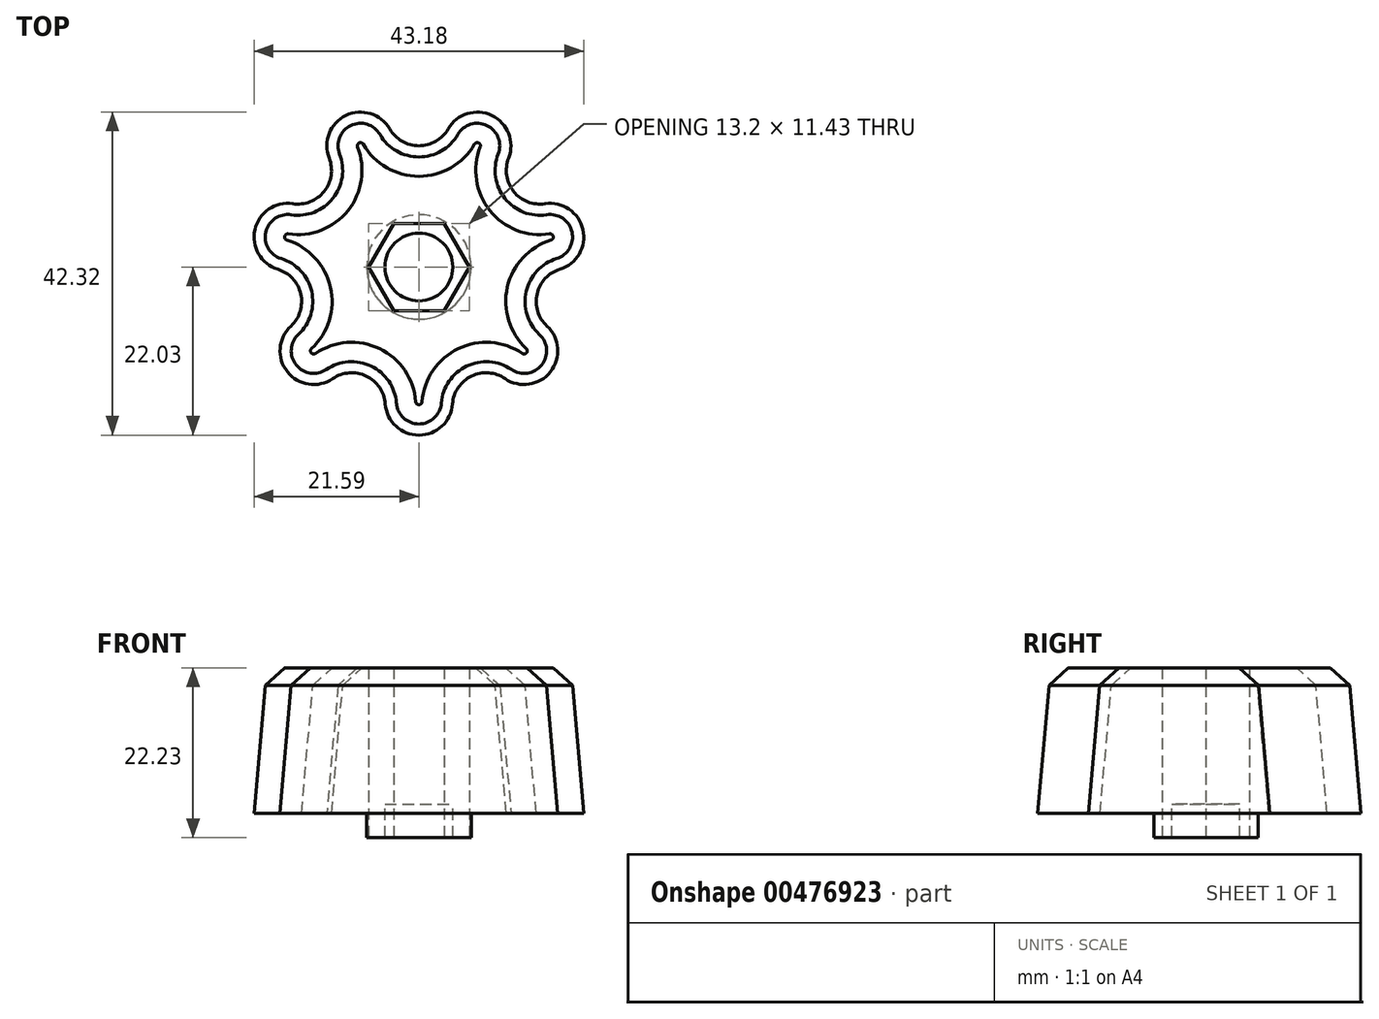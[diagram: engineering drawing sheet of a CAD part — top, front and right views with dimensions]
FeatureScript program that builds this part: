
annotation { "Feature Type Name" : "Feature", "Feature Type Description" : "" }
export const myFeature = defineFeature(function(context is Context, id is Id, definition is map)
    precondition{}
    {
        {
            var Q0;
            Q0=qCreatedBy(makeId("Top.planeOp"),FACE);
            var sketch = newSketch(context, id + "F0", { "sketchPlane" : qUnion([Q0])});
            skCircle(sketch, "E0.cCircle", {"center": v(0, 0) * mm, "radius": 5.72 * mm, "construction": true});
            skLineSegment(sketch, "E0.0", {"start": v(-3.3, 5.72) * mm, "end": v(3.3, 5.72) * mm});
            skLineSegment(sketch, "E0.1", {"start": v(3.3, 5.72) * mm, "end": v(6.6, 0) * mm});
            skLineSegment(sketch, "E0.2", {"start": v(6.6, 0) * mm, "end": v(3.3, -5.71) * mm});
            skLineSegment(sketch, "E0.3", {"start": v(3.3, -5.72) * mm, "end": v(-3.3, -5.72) * mm});
            skLineSegment(sketch, "E0.4", {"start": v(-3.3, -5.72) * mm, "end": v(-6.6, 0) * mm});
            skLineSegment(sketch, "E0.5", {"start": v(-6.6, 0) * mm, "end": v(-3.3, 5.72) * mm});
            skPoint(sketch, "E0.0.midPoint", {"position": v(0, 5.72) * mm});
            skCircle(sketch, "E1.cCircle", {"center": v(0, 0) * mm, "radius": 15.88 * mm, "construction": true});
            skLineSegment(sketch, "E1.0", {"start": v(-7.64, 15.87) * mm, "end": v(7.64, 15.87) * mm, "construction": true});
            skLineSegment(sketch, "E1.1", {"start": v(7.64, 15.88) * mm, "end": v(17.18, 3.92) * mm, "construction": true});
            skLineSegment(sketch, "E1.2", {"start": v(17.18, 3.92) * mm, "end": v(13.78, -10.99) * mm, "construction": true});
            skLineSegment(sketch, "E1.3", {"start": v(13.78, -10.99) * mm, "end": v(0, -17.62) * mm, "construction": true});
            skLineSegment(sketch, "E1.4", {"start": v(0, -17.62) * mm, "end": v(-13.78, -10.99) * mm, "construction": true});
            skLineSegment(sketch, "E1.5", {"start": v(-13.78, -10.99) * mm, "end": v(-17.18, 3.92) * mm, "construction": true});
            skLineSegment(sketch, "E1.6", {"start": v(-17.18, 3.92) * mm, "end": v(-7.64, 15.87) * mm, "construction": true});
            skPoint(sketch, "E1.0.midPoint", {"position": v(0, 15.87) * mm});
            skCircle(sketch, "E2", {"center": v(-7.64, 15.87) * mm, "radius": 4.41 * mm});
            skCircle(sketch, "E3", {"center": v(7.64, 15.87) * mm, "radius": 4.41 * mm});
            skCircle(sketch, "E4", {"center": v(17.18, 3.92) * mm, "radius": 4.41 * mm});
            skCircle(sketch, "E5", {"center": v(13.78, -10.99) * mm, "radius": 4.41 * mm});
            skCircle(sketch, "E6", {"center": v(0, -17.62) * mm, "radius": 4.41 * mm});
            skCircle(sketch, "E7", {"center": v(-13.78, -10.99) * mm, "radius": 4.41 * mm});
            skCircle(sketch, "E8", {"center": v(-17.18, 3.92) * mm, "radius": 4.41 * mm});
            skArc(sketch, "E9", {"start": v(-16.52, 8.29) * mm, "mid": v(-12.41, 9.9) * mm, "end": v(-11.75, 14.26) * mm});
            skArc(sketch, "E10", {"start": v(-3.82, 18.08) * mm, "mid": v(0, 15.87) * mm, "end": v(3.82, 18.08) * mm});
            skArc(sketch, "E11", {"start": v(11.75, 14.26) * mm, "mid": v(12.41, 9.9) * mm, "end": v(16.52, 8.29) * mm});
            skArc(sketch, "E12", {"start": v(18.48, -0.3) * mm, "mid": v(15.48, -3.53) * mm, "end": v(16.78, -7.75) * mm});
            skArc(sketch, "E13", {"start": v(11.29, -14.63) * mm, "mid": v(6.89, -14.3) * mm, "end": v(4.4, -17.95) * mm});
            skArc(sketch, "E14", {"start": v(-4.4, -17.95) * mm, "mid": v(-6.89, -14.3) * mm, "end": v(-11.29, -14.63) * mm});
            skArc(sketch, "E15", {"start": v(-16.78, -7.75) * mm, "mid": v(-15.48, -3.53) * mm, "end": v(-18.48, -0.3) * mm});
            skCircle(sketch, "E16", {"center": v(0, 0) * mm, "radius": 20.29 * mm, "construction": true});
            skCircle(sketch, "E17", {"center": v(0, 0) * mm, "radius": 4.45 * mm});
            skCircle(sketch, "E18", {"center": v(0, 0) * mm, "radius": 9.53 * mm});
            skSolve(sketch);
        }
        {
            var Q0;
            Q0 = qSketchRegion(id + "F0", true);
            var Q1;
            Q1=makeQuery(id+"F0.imprint","IMPRINT",FACE,{"disambiguationData":[TD([[makeQuery(id+"F0.imprint","IMPRINT",EDGE,{"derivedFrom":sQuery(id+"F0.wireOp",EDGE,"E0.0")}),1.0]])]});
            extrude(context, id + "F1", {"entities" : qUnion([Q0, Q1]), "depth" : 19.05 * mm, "hasDraft" : true, "draftAngle" : 5 * degree, "draftPullDirection" : true});
        }
        {
            var Q0;
            Q0=makeQuery(id+"F0.imprint","IMPRINT",FACE,{"disambiguationData":[TD([[makeQuery(id+"F0.imprint","IMPRINT",EDGE,{"derivedFrom":sQuery(id+"F0.wireOp",EDGE,"E0.0")}),1.0]])]});
            var Q1;
            Q1=makeQuery(id+"F1.opExtrude","CAP_FACE",FACE,{"disambiguationData":[OSD([sQuery(id+"F0.wireOp",EDGE,"E0.0"),sQuery(id+"F0.wireOp",EDGE,"E0.1"),sQuery(id+"F0.wireOp",EDGE,"E0.2"),sQuery(id+"F0.wireOp",EDGE,"E0.3"),sQuery(id+"F0.wireOp",EDGE,"E0.4"),sQuery(id+"F0.wireOp",EDGE,"E0.5"),sQuery(id+"F0.wireOp",EDGE,"E2"),sQuery(id+"F0.wireOp",EDGE,"E3"),sQuery(id+"F0.wireOp",EDGE,"E4"),sQuery(id+"F0.wireOp",EDGE,"E5"),sQuery(id+"F0.wireOp",EDGE,"E6"),sQuery(id+"F0.wireOp",EDGE,"E7"),sQuery(id+"F0.wireOp",EDGE,"E8"),sQuery(id+"F0.wireOp",EDGE,"E9"),sQuery(id+"F0.wireOp",EDGE,"E10"),sQuery(id+"F0.wireOp",EDGE,"E11"),sQuery(id+"F0.wireOp",EDGE,"E12"),sQuery(id+"F0.wireOp",EDGE,"E13"),sQuery(id+"F0.wireOp",EDGE,"E14"),sQuery(id+"F0.wireOp",EDGE,"E15")])],"isStart":false});
            extrude(context, id + "F2", {"entities" : qUnion([Q0]), "operationType" : NewBodyOperationType.ADD, "endBound" : BoundingType.UP_TO_SURFACE, "endBoundEntityFace" : qUnion([Q1]), "depth" : 25.4 * mm});
        }
        {
            var Q0;
            Q0=makeQuery(id+"F1.opExtrude","CAP_EDGE",EDGE,{"disambiguationData":[OSD([sQuery(id+"F0.wireOp",EDGE,"E6")])],"isStart":false});
            chamfer(context, id + "F3", {"entities" : qUnion([Q0]), "width" : 2.54 * mm, "tangentPropagation" : true});
        }
        {
            var Q0;
            {var subQ0=sQuery(id+"F0.wireOp",EDGE,"E0.5");var subQ1=sQuery(id+"F0.wireOp",EDGE,"E0.4");var subQ2=sQuery(id+"F0.wireOp",EDGE,"E0.3");var subQ3=sQuery(id+"F0.wireOp",EDGE,"E0.2");var subQ4=sQuery(id+"F0.wireOp",EDGE,"E0.1");var subQ5=sQuery(id+"F0.wireOp",EDGE,"E0.0");Q0=makeQuery(id+"FAqkvu2JH1cbPXJ_1.boolean.opBoolean","MERGE",FACE,{"derivedFrom":[makeQuery(id+"F1.opExtrude","CAP_FACE",FACE,{"disambiguationData":[OSD([subQ5,subQ4,subQ3,subQ2,subQ1,subQ0,sQuery(id+"F0.wireOp",EDGE,"E2"),sQuery(id+"F0.wireOp",EDGE,"E3"),sQuery(id+"F0.wireOp",EDGE,"E4"),sQuery(id+"F0.wireOp",EDGE,"E5"),sQuery(id+"F0.wireOp",EDGE,"E6"),sQuery(id+"F0.wireOp",EDGE,"E7"),sQuery(id+"F0.wireOp",EDGE,"E8"),sQuery(id+"F0.wireOp",EDGE,"E9"),sQuery(id+"F0.wireOp",EDGE,"E10"),sQuery(id+"F0.wireOp",EDGE,"E11"),sQuery(id+"F0.wireOp",EDGE,"E12"),sQuery(id+"F0.wireOp",EDGE,"E13"),sQuery(id+"F0.wireOp",EDGE,"E14"),sQuery(id+"F0.wireOp",EDGE,"E15")])],"isStart":true}),makeQuery(id+"FAqkvu2JH1cbPXJ_1.opExtrude","CAP_FACE",FACE,{"disambiguationData":[OSD([subQ5,subQ4,subQ3,subQ2,subQ1,subQ0,sQuery(id+"F0.wireOp",EDGE,"E17")])],"isStart":true})]});}
            var sketch = newSketch(context, id + "F4", { "sketchPlane" : qUnion([Q0])});
            skCircle(sketch, "E19.0", {"center": v(0, 0) * mm, "radius": 4.45 * mm});
            skCircle(sketch, "E20", {"center": v(0, 0) * mm, "radius": 6.85 * mm});
            skSolve(sketch);
        }
        {
            var Q0;
            Q0=makeQuery(id+"F4.imprint","IMPRINT",FACE,{"disambiguationData":[TD([[makeQuery(id+"F4.imprint","IMPRINT",EDGE,{"derivedFrom":sQuery(id+"F4.wireOp",EDGE,"E20")}),1.0]])]});
            var Q1;
            Q1=makeQuery(id+"F4.imprint","IMPRINT",FACE,{"disambiguationData":[TD([[makeQuery(id+"F4.imprint","IMPRINT",EDGE,{"derivedFrom":sQuery(id+"F4.wireOp",EDGE,"E19.0")}),1.0]])]});
            extrude(context, id + "F5", {"entities" : qUnion([Q0, Q1]), "operationType" : NewBodyOperationType.ADD, "depth" : 3.17 * mm, "hasSecondDirection" : true, "secondDirectionOppositeDirection" : true, "secondDirectionDepth" : 1.2 * mm});
        }
    });
